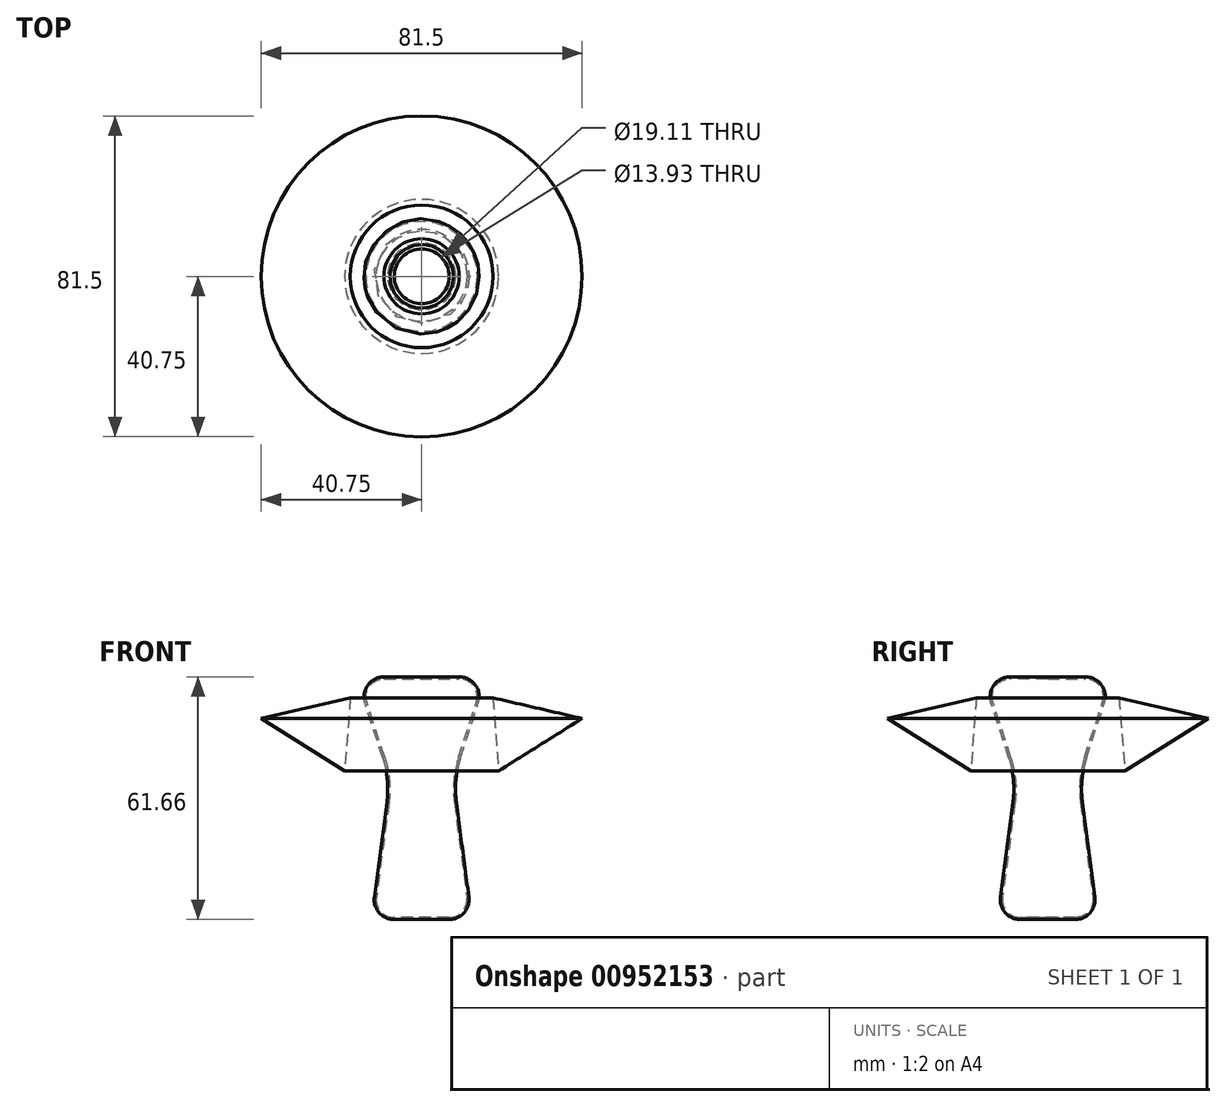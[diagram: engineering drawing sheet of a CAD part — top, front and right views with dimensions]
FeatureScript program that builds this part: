
annotation { "Feature Type Name" : "Feature", "Feature Type Description" : "" }
export const myFeature = defineFeature(function(context is Context, id is Id, definition is map)
    precondition{}
    {
        {
            var Q0;
            Q0=qCreatedBy(makeId("Right.planeOp"),FACE);
            var sketch = newSketch(context, id + "F0", { "sketchPlane" : qUnion([Q0])});
            skLineSegment(sketch, "E0", {"start": v(0, 29.45) * mm, "end": v(0, -32.21) * mm});
            skLineSegment(sketch, "E1", {"start": v(0, -32.21) * mm, "end": v(-12.76, -32.21) * mm});
            skLineSegment(sketch, "E2", {"start": v(-12.76, -32.21) * mm, "end": v(-8.82, -2.42) * mm});
            skLineSegment(sketch, "E3", {"start": v(-9.84, 8.73) * mm, "end": v(-16.54, 29.45) * mm});
            skLineSegment(sketch, "E4", {"start": v(0, 29.45) * mm, "end": v(-2.8, 29.45) * mm});
            skLineSegment(sketch, "E5", {"start": v(-16.54, 29.45) * mm, "end": v(-2.8, 29.45) * mm});
            skPoint(sketch, "E6.visualSharp", {"position": v(-8.07, 3.27) * mm});
            skArc(sketch, "E7.filletArc", {"start": v(-8.82, -2.42) * mm, "mid": v(-8.7, 3.21) * mm, "end": v(-9.84, 8.73) * mm});
            skLineSegment(sketch, "E8", {"start": v(18.14, 24.1) * mm, "end": v(40.75, 18.86) * mm});
            skLineSegment(sketch, "E9", {"start": v(40.75, 18.86) * mm, "end": v(19.56, 5.52) * mm});
            skLineSegment(sketch, "E10", {"start": v(19.56, 5.52) * mm, "end": v(18.14, 24.1) * mm});
            skSolve(sketch);
        }
        {
            var Q0;
            Q0 = qSketchRegion(id + "F0", true);
            var Q1;
            Q1=sQuery(id+"F0.wireOp",EDGE,"E0");
            revolve(context, id + "F1", {"surfaceOperationType" : NewSurfaceOperationType.NEW, "entities" : qUnion([Q0]), "axis" : qUnion([Q1]), "revolveType" : RevolveType.FULL});
        }
        {
            var Q0;
            Q0=makeQuery(id+"F1.opRevolve","SWEPT_EDGE",EDGE,{"disambiguationData":[OSD([sQuery(id+"F0.wireOp",EDGE,"E3"),sQuery(id+"F0.wireOp",EDGE,"E5")])]});
            fillet(context, id + "F2", {"entities" : qUnion([Q0]), "radius" : 5.08 * mm, "tangentPropagation" : true, "allowEdgeOverflow" : false});
        }
        {
            var Q0;
            Q0=makeQuery(id+"F1.opRevolve","SWEPT_EDGE",EDGE,{"disambiguationData":[OSD([sQuery(id+"F0.wireOp",EDGE,"E1"),sQuery(id+"F0.wireOp",EDGE,"E2")])]});
            fillet(context, id + "F3", {"entities" : qUnion([Q0]), "radius" : 5.08 * mm, "tangentPropagation" : true, "allowEdgeOverflow" : false});
        }
        {
            var Q0;
            Q0=makeQuery(id+"F1.opRevolve","SWEPT_FACE",FACE,{"disambiguationData":[OSD([sQuery(id+"F0.wireOp",EDGE,"E4"),sQuery(id+"F0.wireOp",EDGE,"E5")])]});
            var Q1;
            Q1=makeQuery(id+"F1.opRevolve","SWEPT_FACE",FACE,{"disambiguationData":[OSD([sQuery(id+"F0.wireOp",EDGE,"E1")])]});
            shell(context, id + "F4", {"entities" : qUnion([Q0, Q1]), "thickness" : 0.5 * mm});
        }
    });
